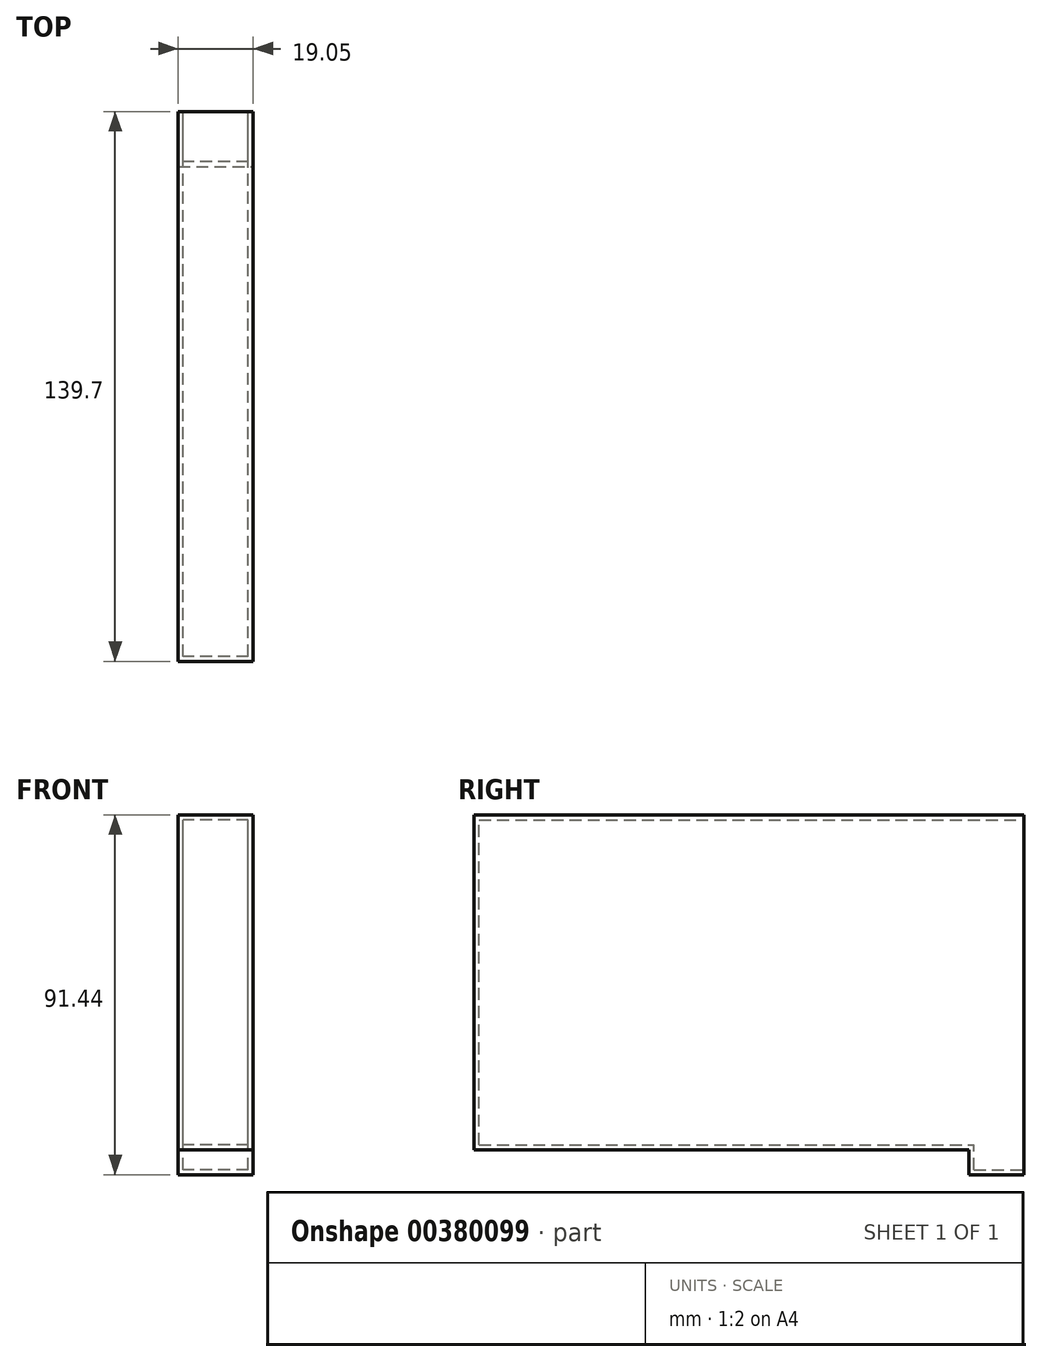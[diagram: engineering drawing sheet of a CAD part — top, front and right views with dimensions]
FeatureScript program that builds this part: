
annotation { "Feature Type Name" : "Feature", "Feature Type Description" : "" }
export const myFeature = defineFeature(function(context is Context, id is Id, definition is map)
    precondition{}
    {
        {
            var Q0;
            Q0=qCreatedBy(makeId("Right.planeOp"),FACE);
            var sketch = newSketch(context, id + "F0", { "sketchPlane" : qUnion([Q0])});
            skLineSegment(sketch, "E0.bottom", {"start": v(69.85, -45.72) * mm, "end": v(-69.85, -45.72) * mm});
            skLineSegment(sketch, "E0.top", {"start": v(69.85, 45.72) * mm, "end": v(-69.85, 45.72) * mm});
            skLineSegment(sketch, "E0.left", {"start": v(69.85, -45.72) * mm, "end": v(69.85, 45.72) * mm});
            skLineSegment(sketch, "E0.right", {"start": v(-69.85, -45.72) * mm, "end": v(-69.85, 45.72) * mm});
            skPoint(sketch, "E0.middle", {"position": v(0, 0) * mm});
            skSolve(sketch);
        }
        {
            var Q0;
            Q0 = qSketchRegion(id + "F0", true);
            extrude(context, id + "F1", {"entities" : qUnion([Q0]), "depth" : 19.05 * mm});
        }
        {
            var Q0;
            Q0=makeQuery(id+"F1.opExtrude","CAP_FACE",FACE,{"disambiguationData":[OSD([sQuery(id+"F0.wireOp",EDGE,"E0.bottom"),sQuery(id+"F0.wireOp",EDGE,"E0.top"),sQuery(id+"F0.wireOp",EDGE,"E0.left"),sQuery(id+"F0.wireOp",EDGE,"E0.right")])],"isStart":false});
            var sketch = newSketch(context, id + "F2", { "sketchPlane" : qUnion([Q0])});
            skLineSegment(sketch, "E1", {"start": v(69.85, -45.72) * mm, "end": v(55.88, -45.72) * mm});
            skLineSegment(sketch, "E2", {"start": v(55.88, -45.72) * mm, "end": v(55.88, -39.37) * mm});
            skLineSegment(sketch, "E3", {"start": v(55.88, -39.37) * mm, "end": v(-69.85, -39.37) * mm});
            skLineSegment(sketch, "E4", {"start": v(-69.85, -39.37) * mm, "end": v(-69.85, -45.72) * mm});
            skLineSegment(sketch, "E5", {"start": v(-69.85, -45.72) * mm, "end": v(55.88, -45.72) * mm});
            skSolve(sketch);
        }
        {
            var Q0;
            Q0 = qSketchRegion(id + "F2", true);
            extrude(context, id + "F3", {"entities" : qUnion([Q0]), "operationType" : NewBodyOperationType.REMOVE, "oppositeDirection" : true, "depth" : 25.4 * mm});
        }
        {
            var Q0;
            Q0=makeQuery(id+"F1.opExtrude","SWEPT_FACE",FACE,{"disambiguationData":[OSD([sQuery(id+"F0.wireOp",EDGE,"E0.left")])]});
            var sketch = newSketch(context, id + "F4", { "sketchPlane" : qUnion([Q0])});
            skLineSegment(sketch, "E6.bottom", {"start": v(-19.05, -45.72) * mm, "end": v(-17.78, -45.72) * mm});
            skLineSegment(sketch, "E6.top", {"start": v(-19.05, -44.45) * mm, "end": v(-17.78, -44.45) * mm});
            skLineSegment(sketch, "E6.left", {"start": v(-19.05, -45.72) * mm, "end": v(-19.05, -44.45) * mm});
            skLineSegment(sketch, "E6.right", {"start": v(-17.78, -45.72) * mm, "end": v(-17.78, -44.45) * mm});
            skLineSegment(sketch, "E7.bottom", {"start": v(-17.78, -44.45) * mm, "end": v(-1.27, -44.45) * mm});
            skLineSegment(sketch, "E7.top", {"start": v(-17.78, 44.45) * mm, "end": v(-1.27, 44.45) * mm});
            skLineSegment(sketch, "E7.left", {"start": v(-17.78, -44.45) * mm, "end": v(-17.78, 44.45) * mm});
            skLineSegment(sketch, "E7.right", {"start": v(-1.27, -44.45) * mm, "end": v(-1.27, 44.45) * mm});
            skSolve(sketch);
        }
        {
            var Q0;
            Q0=makeQuery(id+"F4.imprint","IMPRINT",FACE,{"disambiguationData":[TD([[makeQuery(id+"F4.imprint","IMPRINT",EDGE,{"derivedFrom":sQuery(id+"F4.wireOp",EDGE,"E7.bottom")}),1.0]])]});
            extrude(context, id + "F5", {"entities" : qUnion([Q0]), "operationType" : NewBodyOperationType.REMOVE, "oppositeDirection" : true, "depth" : 12.7 * mm});
        }
        {
            var Q0;
            Q0=makeQuery(id+"F5.boolean.opBoolean","COPY",FACE,{"derivedFrom":makeQuery(id+"F5.opExtrude","CAP_FACE",FACE,{"disambiguationData":[OSD([sQuery(id+"F4.wireOp",EDGE,"E7.bottom"),sQuery(id+"F4.wireOp",EDGE,"E7.top"),sQuery(id+"F4.wireOp",EDGE,"E7.left"),sQuery(id+"F4.wireOp",EDGE,"E7.right")])],"isStart":false})});
            var sketch = newSketch(context, id + "F6", { "sketchPlane" : qUnion([Q0])});
            skLineSegment(sketch, "E8.bottom", {"start": v(-17.78, 44.45) * mm, "end": v(-1.27, 44.45) * mm});
            skLineSegment(sketch, "E8.top", {"start": v(-17.78, -38.1) * mm, "end": v(-1.27, -38.1) * mm});
            skLineSegment(sketch, "E8.left", {"start": v(-17.78, 44.45) * mm, "end": v(-17.78, -38.1) * mm});
            skLineSegment(sketch, "E8.right", {"start": v(-1.27, 44.45) * mm, "end": v(-1.27, -38.1) * mm});
            skSolve(sketch);
        }
        {
            var Q0;
            Q0 = qSketchRegion(id + "F6", true);
            extrude(context, id + "F7", {"entities" : qUnion([Q0]), "operationType" : NewBodyOperationType.REMOVE, "oppositeDirection" : true, "depth" : 125.73 * mm});
        }
    });
